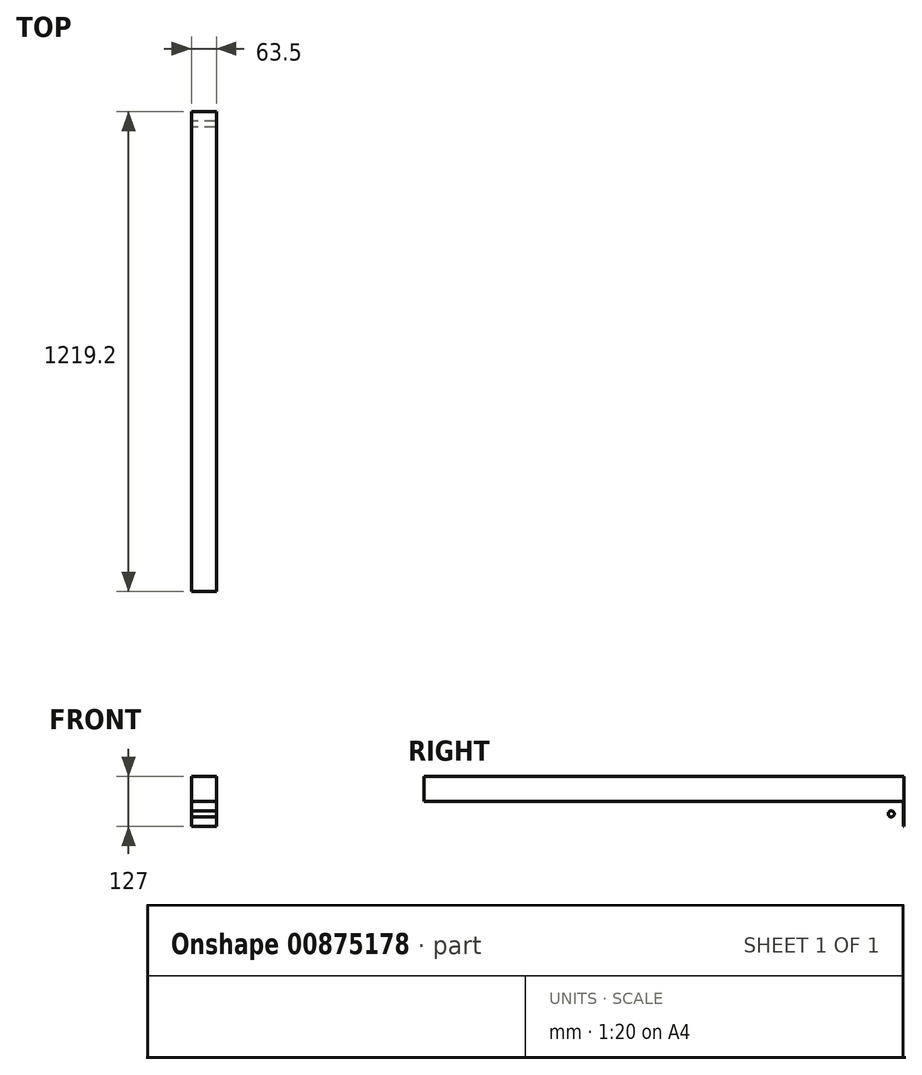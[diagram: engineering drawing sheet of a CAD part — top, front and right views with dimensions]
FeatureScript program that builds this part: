
annotation { "Feature Type Name" : "Feature", "Feature Type Description" : "" }
export const myFeature = defineFeature(function(context is Context, id is Id, definition is map)
    precondition{}
    {
        {
            var Q0;
            Q0=qCreatedBy(makeId("Front.planeOp"),FACE);
            var sketch = newSketch(context, id + "F0", { "sketchPlane" : qUnion([Q0])});
            skLineSegment(sketch, "E0.bottom", {"start": v(-118.73, 38.49) * mm, "end": v(-55.23, 38.49) * mm});
            skLineSegment(sketch, "E0.top", {"start": v(-118.73, -25.01) * mm, "end": v(-55.23, -25.01) * mm});
            skLineSegment(sketch, "E0.left", {"start": v(-118.73, 38.49) * mm, "end": v(-118.73, -25.01) * mm});
            skLineSegment(sketch, "E0.right", {"start": v(-55.23, 38.49) * mm, "end": v(-55.23, -25.01) * mm});
            skSolve(sketch);
        }
        {
            var Q0;
            Q0=makeQuery(id+"F0.imprint","IMPRINT",FACE,{"disambiguationData":[TD([[makeQuery(id+"F0.imprint","IMPRINT",EDGE,{"derivedFrom":sQuery(id+"F0.wireOp",EDGE,"E0.bottom")}),-1.0]])]});
            extrude(context, id + "F1", {"entities" : qUnion([Q0]), "depth" : 1219.2 * mm, "offsetDistance" : 25.4 * mm});
        }
        {
            var Q0;
            Q0=makeQuery(id+"F1.opExtrude","SWEPT_FACE",FACE,{"disambiguationData":[OSD([sQuery(id+"F0.wireOp",EDGE,"E0.top")])]});
            var sketch = newSketch(context, id + "F2", { "sketchPlane" : qUnion([Q0])});
            skLineSegment(sketch, "E1.bottom", {"start": v(-118.73, 0) * mm, "end": v(-55.23, 0) * mm});
            skLineSegment(sketch, "E1.top", {"start": v(-118.73, 64.37) * mm, "end": v(-55.23, 64.37) * mm});
            skLineSegment(sketch, "E1.left", {"start": v(-118.73, 0) * mm, "end": v(-118.73, 64.37) * mm});
            skLineSegment(sketch, "E1.right", {"start": v(-55.23, 0) * mm, "end": v(-55.23, 64.37) * mm});
            skSolve(sketch);
        }
        {
            var Q0;
            Q0=makeQuery(id+"F2.imprint","IMPRINT",FACE,{"disambiguationData":[TD([[makeQuery(id+"F2.imprint","IMPRINT",EDGE,{"derivedFrom":sQuery(id+"F2.wireOp",EDGE,"E1.bottom")}),1.0]])]});
            extrude(context, id + "F3", {"entities" : qUnion([Q0]), "operationType" : NewBodyOperationType.ADD, "depth" : 63.5 * mm, "offsetDistance" : 25.4 * mm});
        }
        {
            var Q0;
            Q0=makeQuery(id+"F3.boolean.opBoolean","MERGE",FACE,{"derivedFrom":[makeQuery(id+"F1.opExtrude","SWEPT_FACE",FACE,{"disambiguationData":[OSD([sQuery(id+"F0.wireOp",EDGE,"E0.left")])]}),makeQuery(id+"F3.opExtrude","SWEPT_FACE",FACE,{"disambiguationData":[OSD([sQuery(id+"F2.wireOp",EDGE,"E1.left")])]})]});
            var sketch = newSketch(context, id + "F4", { "sketchPlane" : qUnion([Q0])});
            skLineSegment(sketch, "E2.bottom", {"start": v(64.37, -88.51) * mm, "end": v(0.87, -88.51) * mm});
            skLineSegment(sketch, "E2.top", {"start": v(64.37, -25.01) * mm, "end": v(0.87, -25.01) * mm});
            skLineSegment(sketch, "E2.left", {"start": v(64.37, -88.51) * mm, "end": v(64.37, -25.01) * mm});
            skLineSegment(sketch, "E2.right", {"start": v(0.87, -88.51) * mm, "end": v(0.87, -25.01) * mm});
            skLineSegment(sketch, "E3", {"start": v(64.37, -25.01) * mm, "end": v(32.62, -25.01) * mm});
            skLineSegment(sketch, "E4", {"start": v(32.62, -25.01) * mm, "end": v(32.19, -88.51) * mm});
            skCircle(sketch, "E5", {"center": v(32.4, -56.76) * mm, "radius": 7.62 * mm});
            skSolve(sketch);
        }
        {
            var Q0;
            {var subQ0=sQuery(id+"F4.wireOp",EDGE,"E5");var subQ1=sQuery(id+"F4.wireOp",EDGE,"E4");var subQ2=makeQuery(id+"F4.imprint","INTERSECT",VERTEX,{"disambiguationData":[OD(0.0)],"derivedFrom":[subQ1,subQ0]});Q0=makeQuery(id+"F4.imprint","IMPRINT",FACE,{"disambiguationData":[TD([[makeQuery(id+"F4.imprint","IMPRINT",EDGE,{"disambiguationData":[TD([[subQ2,-1.0]])],"derivedFrom":subQ1}),1.0]])]});}
            var Q1;
            {var subQ0=sQuery(id+"F4.wireOp",EDGE,"E5");var subQ1=sQuery(id+"F4.wireOp",EDGE,"E4");var subQ2=makeQuery(id+"F4.imprint","INTERSECT",VERTEX,{"disambiguationData":[OD(0.0)],"derivedFrom":[subQ1,subQ0]});Q1=makeQuery(id+"F4.imprint","IMPRINT",FACE,{"disambiguationData":[TD([[makeQuery(id+"F4.imprint","IMPRINT",EDGE,{"disambiguationData":[TD([[subQ2,-1.0]])],"derivedFrom":subQ1}),-1.0]])]});}
            extrude(context, id + "F5", {"entities" : qUnion([Q0, Q1]), "operationType" : NewBodyOperationType.REMOVE, "oppositeDirection" : true, "depth" : 76.2 * mm, "offsetDistance" : 25.4 * mm});
        }
    });
